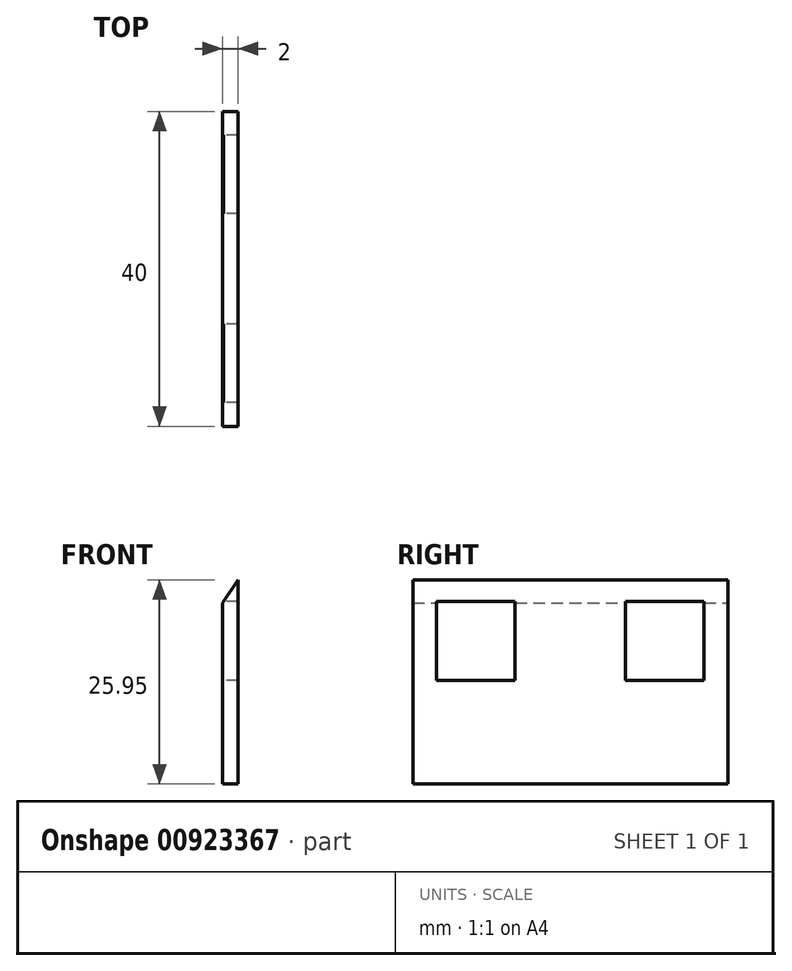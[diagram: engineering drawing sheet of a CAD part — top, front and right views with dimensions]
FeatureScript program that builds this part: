
annotation { "Feature Type Name" : "Feature", "Feature Type Description" : "" }
export const myFeature = defineFeature(function(context is Context, id is Id, definition is map)
    precondition{}
    {
        {
            var Q0;
            Q0=qCreatedBy(makeId("Right.planeOp"),FACE);
            var sketch = newSketch(context, id + "F0", { "sketchPlane" : qUnion([Q0])});
            skLineSegment(sketch, "E0.bottom", {"start": v(20, -13.1) * mm, "end": v(-20, -13.1) * mm});
            skLineSegment(sketch, "E0.top", {"start": v(20, 13.1) * mm, "end": v(-20, 13.1) * mm});
            skLineSegment(sketch, "E0.left", {"start": v(20, -13.1) * mm, "end": v(20, 13.1) * mm});
            skLineSegment(sketch, "E0.right", {"start": v(-20, -13.1) * mm, "end": v(-20, 13.1) * mm});
            skPoint(sketch, "E0.middle", {"position": v(0, 0) * mm});
            skLineSegment(sketch, "E1.bottom", {"start": v(-17, 10.1) * mm, "end": v(-7, 10.1) * mm});
            skLineSegment(sketch, "E1.top", {"start": v(-17, 0.1) * mm, "end": v(-7, 0.1) * mm});
            skLineSegment(sketch, "E1.left", {"start": v(-17, 10.1) * mm, "end": v(-17, 0.1) * mm});
            skLineSegment(sketch, "E1.right", {"start": v(-7, 10.1) * mm, "end": v(-7, 0.1) * mm});
            skLineSegment(sketch, "E2.bottom", {"start": v(7, 0.1) * mm, "end": v(17, 0.1) * mm});
            skLineSegment(sketch, "E2.top", {"start": v(7, 10.1) * mm, "end": v(17, 10.1) * mm});
            skLineSegment(sketch, "E2.left", {"start": v(7, 0.1) * mm, "end": v(7, 10.1) * mm});
            skLineSegment(sketch, "E2.right", {"start": v(17, 0.1) * mm, "end": v(17, 10.1) * mm});
            skSolve(sketch);
        }
        {
            var Q0;
            Q0=makeQuery(id+"F0.imprint","IMPRINT",FACE,{"disambiguationData":[TD([[makeQuery(id+"F0.imprint","IMPRINT",EDGE,{"derivedFrom":sQuery(id+"F0.wireOp",EDGE,"E0.bottom")}),-1.0]])]});
            extrude(context, id + "F1", {"entities" : qUnion([Q0]), "depth" : 2 * mm, "offsetDistance" : 25 * mm});
        }
        {
            var Q0;
            Q0=makeQuery(id+"F1.opExtrude","CAP_EDGE",EDGE,{"disambiguationData":[OSD([sQuery(id+"F0.wireOp",EDGE,"E0.top")])],"isStart":true});
            chamfer(context, id + "F2", {"entities" : qUnion([Q0]), "chamferType" : ChamferType.TWO_OFFSETS, "width1" : 2.17 * mm, "oppositeDirection" : false, "width2" : 3.2 * mm, "tangentPropagation" : true});
        }
    });
